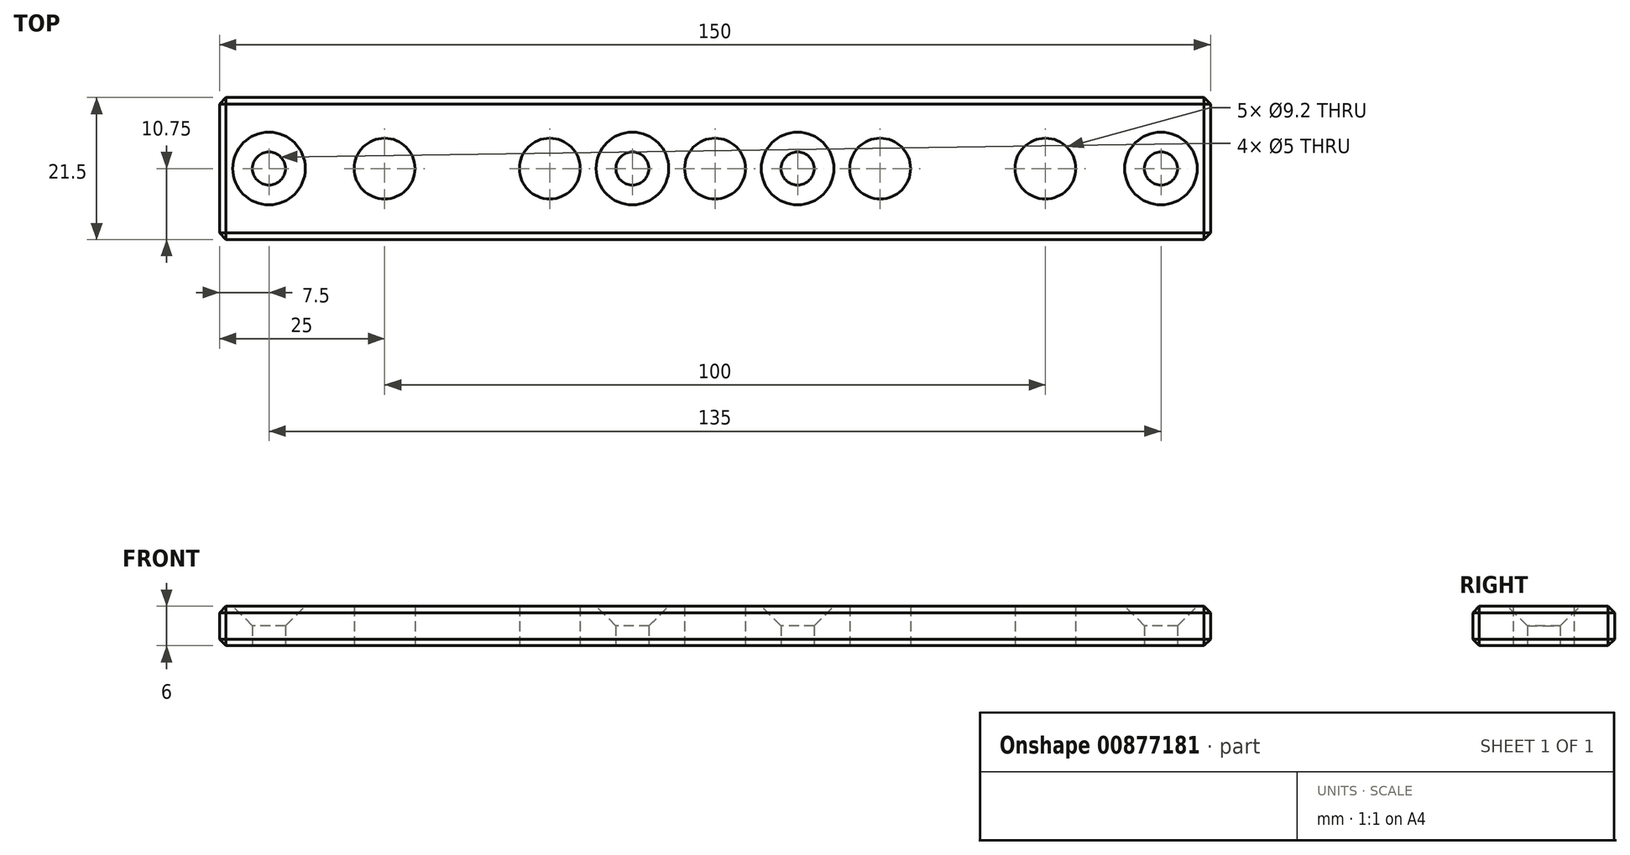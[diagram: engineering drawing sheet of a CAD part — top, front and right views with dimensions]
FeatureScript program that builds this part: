
annotation { "Feature Type Name" : "Feature", "Feature Type Description" : "" }
export const myFeature = defineFeature(function(context is Context, id is Id, definition is map)
    precondition{}
    {
        {
            var Q0;
            Q0=qCreatedBy(makeId("Top.planeOp"),FACE);
            var sketch = newSketch(context, id + "F0", { "sketchPlane" : qUnion([Q0])});
            skLineSegment(sketch, "E0.bottom", {"start": v(75, 10.75) * mm, "end": v(-75, 10.75) * mm});
            skLineSegment(sketch, "E0.top", {"start": v(75, -10.75) * mm, "end": v(-75, -10.75) * mm});
            skLineSegment(sketch, "E0.left", {"start": v(75, 10.75) * mm, "end": v(75, -10.75) * mm});
            skLineSegment(sketch, "E0.right", {"start": v(-75, 10.75) * mm, "end": v(-75, -10.75) * mm});
            skPoint(sketch, "E0.middle", {"position": v(0, 0) * mm});
            skLineSegment(sketch, "E1", {"start": v(0, 0) * mm, "end": v(-75, 0) * mm});
            skCircle(sketch, "E2", {"center": v(0, 0) * mm, "radius": 4.6 * mm});
            skCircle(sketch, "E3", {"center": v(-12.5, 0) * mm, "radius": 2.5 * mm});
            skCircle(sketch, "E4", {"center": v(-25, 0) * mm, "radius": 4.6 * mm});
            skCircle(sketch, "E5", {"center": v(-50, 0) * mm, "radius": 4.6 * mm});
            skCircle(sketch, "E6", {"center": v(-67.5, 0) * mm, "radius": 2.5 * mm});
            skLineSegment(sketch, "E7", {"start": v(0, 0) * mm, "end": v(0, 38.81) * mm});
            skCircle(sketch, "E8.MirrorC", {"center": v(25, 0) * mm, "radius": 4.6 * mm});
            skCircle(sketch, "E9.MirrorC", {"center": v(12.5, 0) * mm, "radius": 2.5 * mm});
            skCircle(sketch, "E10.MirrorC", {"center": v(50, 0) * mm, "radius": 4.6 * mm});
            skCircle(sketch, "E11.MirrorC", {"center": v(67.5, 0) * mm, "radius": 2.5 * mm});
            skSolve(sketch);
        }
        {
            var Q0;
            {var subQ21=sQuery(id+"F0.wireOp",EDGE,"E0.top");Q0=makeQuery(id+"F0.imprint","IMPRINT",FACE,{"disambiguationData":[TD([[makeQuery(id+"F0.imprint","IMPRINT",EDGE,{"derivedFrom":subQ21}),-1.0]])]});}
            var Q1;
            {var subQ12=sQuery(id+"F0.wireOp",EDGE,"E0.right");var subQ13=sQuery(id+"F0.wireOp",EDGE,"E0.bottom");var subQ14=makeQuery(id+"F0.imprint","INTERSECT",VERTEX,{"derivedFrom":[subQ13,subQ12]});Q1=makeQuery(id+"F0.imprint","IMPRINT",FACE,{"disambiguationData":[TD([[makeQuery(id+"F0.imprint","IMPRINT",EDGE,{"disambiguationData":[TD([[subQ14,1.0]])],"derivedFrom":subQ13}),1.0]])]});}
            extrude(context, id + "F1", {"entities" : qUnion([Q0, Q1]), "depth" : 6 * mm, "offsetDistance" : 25 * mm});
        }
        {
            var Q0;
            Q0=makeQuery(id+"F1.opExtrude","CAP_EDGE",EDGE,{"disambiguationData":[OSD([sQuery(id+"F0.wireOp",EDGE,"E0.bottom")])],"isStart":false});
            var Q1;
            Q1=makeQuery(id+"F1.opExtrude","CAP_EDGE",EDGE,{"disambiguationData":[OSD([sQuery(id+"F0.wireOp",EDGE,"E0.top")])],"isStart":true});
            var Q2;
            Q2=makeQuery(id+"F1.opExtrude","CAP_EDGE",EDGE,{"disambiguationData":[OSD([sQuery(id+"F0.wireOp",EDGE,"E0.bottom")])],"isStart":true});
            var Q3;
            Q3=makeQuery(id+"F1.opExtrude","CAP_EDGE",EDGE,{"disambiguationData":[OSD([sQuery(id+"F0.wireOp",EDGE,"E0.right")])],"isStart":true});
            var Q4;
            Q4=makeQuery(id+"F1.opExtrude","CAP_EDGE",EDGE,{"disambiguationData":[OSD([sQuery(id+"F0.wireOp",EDGE,"E0.right")])],"isStart":false});
            var Q5;
            Q5=makeQuery(id+"F1.opExtrude","CAP_EDGE",EDGE,{"disambiguationData":[OSD([sQuery(id+"F0.wireOp",EDGE,"E0.left")])],"isStart":true});
            var Q6;
            Q6=makeQuery(id+"F1.opExtrude","CAP_EDGE",EDGE,{"disambiguationData":[OSD([sQuery(id+"F0.wireOp",EDGE,"E0.left")])],"isStart":false});
            var Q7;
            Q7=makeQuery(id+"F1.opExtrude","SWEPT_EDGE",EDGE,{"disambiguationData":[OSD([sQuery(id+"F0.wireOp",EDGE,"E0.bottom"),sQuery(id+"F0.wireOp",EDGE,"E0.right")])]});
            var Q8;
            Q8=makeQuery(id+"F1.opExtrude","SWEPT_EDGE",EDGE,{"disambiguationData":[OSD([sQuery(id+"F0.wireOp",EDGE,"E0.top"),sQuery(id+"F0.wireOp",EDGE,"E0.right")])]});
            var Q9;
            Q9=makeQuery(id+"F1.opExtrude","CAP_EDGE",EDGE,{"disambiguationData":[OSD([sQuery(id+"F0.wireOp",EDGE,"E0.top")])],"isStart":false});
            var Q10;
            Q10=makeQuery(id+"F1.opExtrude","SWEPT_EDGE",EDGE,{"disambiguationData":[OSD([sQuery(id+"F0.wireOp",EDGE,"E0.top"),sQuery(id+"F0.wireOp",EDGE,"E0.left")])]});
            var Q11;
            Q11=makeQuery(id+"F1.opExtrude","SWEPT_EDGE",EDGE,{"disambiguationData":[OSD([sQuery(id+"F0.wireOp",EDGE,"E0.bottom"),sQuery(id+"F0.wireOp",EDGE,"E0.left")])]});
            chamfer(context, id + "F2", {"entities" : qUnion([Q0, Q1, Q2, Q3, Q4, Q5, Q6, Q7, Q8, Q9, Q10, Q11]), "width" : 1 * mm, "tangentPropagation" : true});
        }
        {
            var Q0;
            Q0=makeQuery(id+"F1.opExtrude","CAP_EDGE",EDGE,{"disambiguationData":[OSD([sQuery(id+"F0.wireOp",EDGE,"E6")])],"isStart":false});
            var Q1;
            Q1=makeQuery(id+"F1.opExtrude","CAP_EDGE",EDGE,{"disambiguationData":[OSD([sQuery(id+"F0.wireOp",EDGE,"E3")])],"isStart":false});
            var Q2;
            Q2=makeQuery(id+"F1.opExtrude","CAP_EDGE",EDGE,{"disambiguationData":[OSD([sQuery(id+"F0.wireOp",EDGE,"E9.MirrorC")])],"isStart":false});
            var Q3;
            Q3=makeQuery(id+"F1.opExtrude","CAP_EDGE",EDGE,{"disambiguationData":[OSD([sQuery(id+"F0.wireOp",EDGE,"E11.MirrorC")])],"isStart":false});
            chamfer(context, id + "F3", {"entities" : qUnion([Q0, Q1, Q2, Q3]), "width" : 3 * mm, "tangentPropagation" : true});
        }
    });
